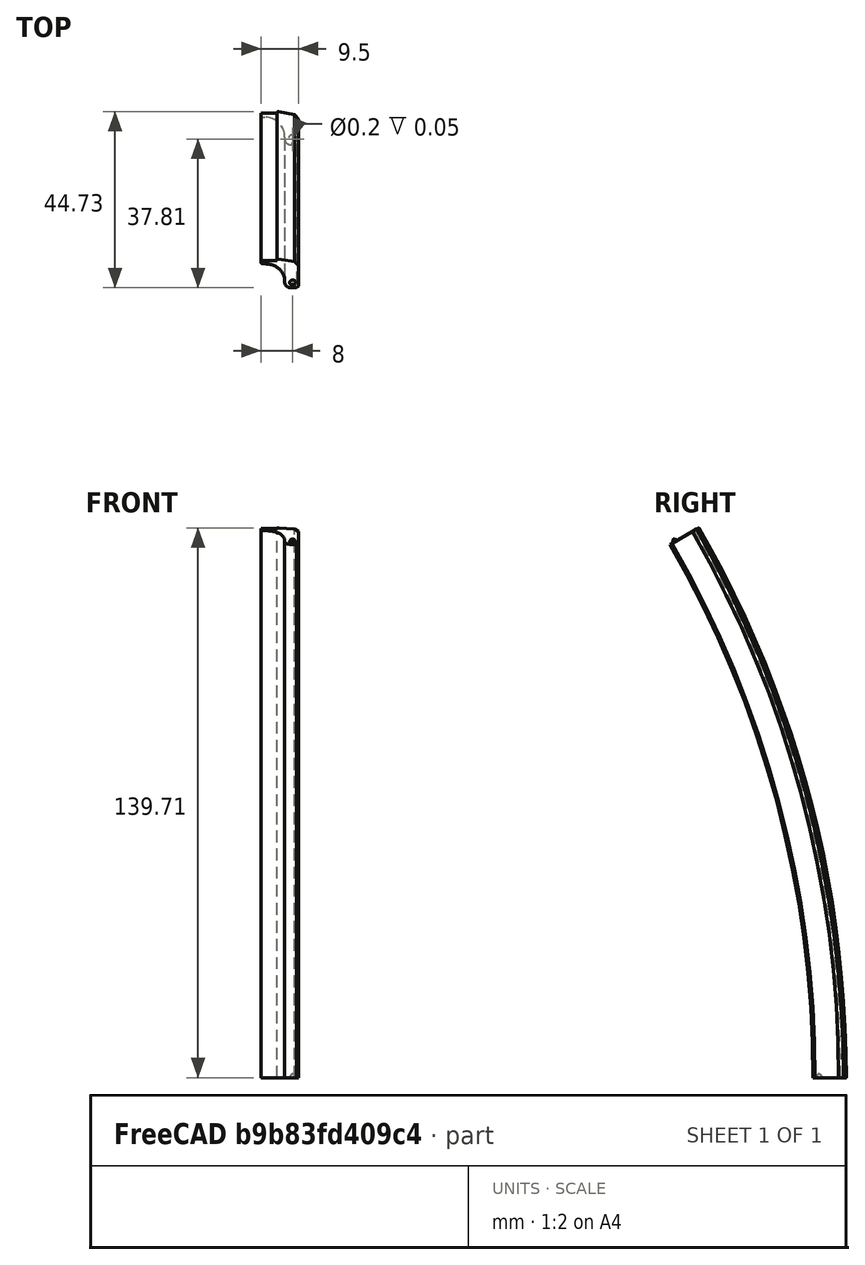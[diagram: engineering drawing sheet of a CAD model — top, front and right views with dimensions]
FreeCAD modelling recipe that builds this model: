
FCSTD DOCUMENT  (FreeCAD 0.16R)
Label: BeadBlock1.2
License: All rights reserved
LicenseURL: http://en.wikipedia.org/wiki/All_rights_reserved
objects: PartDesign::Fillet×4, PartDesign::Chamfer×4, Sketcher::SketchObject×3, PartDesign::Revolution×1, PartDesign::Pad×1, PartDesign::Pocket×1, Mesh::Feature×1
note: 17 computed .brp shape members not serialized (recipe doc carries the construction recipe); baked Part::Feature solids carry a one-line shape summary decoded from their .brp

FEATURE [Sketcher::SketchObject] Sketch
  sketch-geometry (8):
    g0: LineSegment StartX=0 StartY=279 StartZ=0 EndX=4 EndY=279 EndZ=0
    g1: LineSegment StartX=4 StartY=279 StartZ=0 EndX=4 EndY=279.5 EndZ=0
    g2: LineSegment StartX=0 StartY=278 StartZ=0 EndX=0 EndY=279 EndZ=0
    g3: LineSegment StartX=0 StartY=278 StartZ=0 EndX=6 EndY=278 EndZ=0
    g4: LineSegment StartX=6 StartY=278 StartZ=0 EndX=6 EndY=271 EndZ=0
    g5: LineSegment StartX=6 StartY=271 StartZ=0 EndX=9.5 EndY=271 EndZ=0
    g6: LineSegment StartX=9.5 StartY=271 StartZ=0 EndX=9.5 EndY=278.5 EndZ=0
    g7: LineSegment StartX=4 StartY=279.5 StartZ=0 EndX=9.5 EndY=278.5 EndZ=0
  constraints (24):
    c: Horizontal(g0)
    c: PointOnObject(g0,g-2)
    c: DistanceY(g0) = 279
    c: Distance(g0) = 4
    c: Coincident(g1,g0)
    c: Vertical(g1)
    c: Distance(g1) = 0.5
    c: Vertical(g2)
    c: Coincident(g2,g0)
    c: Distance(g2) = 1
    c: Horizontal(g3)
    c: Coincident(g3,g2)
    c: Distance(g3) = 6
    c: Vertical(g4)
    c: Coincident(g4,g3)
    c: Distance(g4) = 7
    c: Horizontal(g5)
    c: Coincident(g5,g4)
    c: Distance(g5) = 3.5
    c: Vertical(g6)
    c: Coincident(g5,g6)
    c: Distance(g6) = 7.5
    c: Coincident(g7,g1)
    c: Coincident(g7,g6)
FEATURE [PartDesign::Revolution] Revolution
  Angle = 30
  Axis = (1,0,0)
  Base = (0,0,0)
  ReferenceAxis = -> Sketch [H_Axis]
  Sketch = -> Sketch
FEATURE [PartDesign::Fillet] Fillet
  Base = -> Revolution [Edge17]
  Radius = 5
FEATURE [PartDesign::Fillet] Fillet001
  Base = -> Fillet [Edge26]
  Radius = 0.4
FEATURE [PartDesign::Fillet] Fillet002
  Base = -> Fillet001 [Edge20]
  Radius = 1.5
FEATURE [PartDesign::Fillet] Fillet003
  Base = -> Fillet002 [Edge27]
  Radius = 0.3
FEATURE [PartDesign::Chamfer] Chamfer
  Base = -> Fillet003 [Edge30]
  Size = 0.5
FEATURE [PartDesign::Chamfer] Chamfer001
  Base = -> Chamfer [Edge21]
  Size = 1
FEATURE [Sketcher::SketchObject] Sketch001
  ExternalGeometry = -> [Chamfer001]
  Placement = pos=(0,0,0) rot=(1,0,0;0.523599rad)
  Support = -> Chamfer001 [Face16]
  sketch-geometry (1):
    g0: Circle CenterX=8 CenterY=272.5 CenterZ=0 NormalX=0 NormalY=0 NormalZ=1 Radius=0.75
  constraints (3):
    c: Radius(g0) = 0.75
    c: Distance(g0,g-3) = 1.5
    c: Distance(g0,g-4) = 1.5
FEATURE [PartDesign::Pad] Pad
  Length = 0.75
  Length2 = 100
  Sketch = -> Sketch001
  Type = 0
FEATURE [PartDesign::Chamfer] Chamfer002
  Base = -> Pad [Edge1]
  Size = 0.72
FEATURE [Sketcher::SketchObject] Sketch002
  ExternalGeometry = -> [Chamfer002]
  Placement = pos=(0,0,0) rot=(1,0,0;3.14159rad)
  Support = -> Chamfer002 [Face19]
  sketch-geometry (1):
    g0: Circle CenterX=8 CenterY=-272.5 CenterZ=0 NormalX=0 NormalY=0 NormalZ=1 Radius=0.1
  constraints (3):
    c: Distance(g0,g-4) = 1.5
    c: Distance(g0,g-3) = 1.5
    c: Radius(g0) = 0.1
FEATURE [PartDesign::Pocket] Pocket
  Length = 1
  Sketch = -> Sketch002
  Type = 0
FEATURE [PartDesign::Chamfer] Chamfer003
  Base = -> Pocket [Edge48]
  Size = 0.95
FEATURE [Mesh::Feature] Mesh  label="Chamfer003 (Meshed)"
